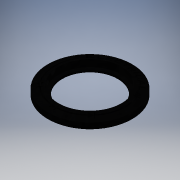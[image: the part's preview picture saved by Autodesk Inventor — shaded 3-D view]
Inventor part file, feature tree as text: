
AUTODESK INVENTOR PART (.ipt)
format: ipt  version: 2016 (Build 200138000, 138)  size: 675,840 bytes
history: native  units: in
note: dims shown in document units (in); Inventor stores cm internally (conversion verified against a paired STEP export)
features: sketch x3, extrude x2, projected_geometry x2, revolve x1
ambient origin geometry x8: Origin, YZ Plane, XZ Plane, XY Plane, X Axis, Y Axis, Z Axis, Center Point
bodies: Solid1 (feature_tree)
feature tree (8):
  revolve  "Revolution1"  [1 undecoded]
  extrude  "Extrusion1"  Depth=0.1in
  extrude  "Extrusion2"  Depth=0.275in
  sketch  "Sketch1"  dims[d0=0.8265in d1=0.175in]
  sketch  "Sketch2"  dims[d2=0.05in d3=0.1in]
  projected_geometry  "Projected Loop1"
  sketch  "Sketch3"  dims[d4=0.15in d5=0.275in d6=90.0deg d7=0.1in d18=0.05in d21=0.025in d22=0.125in d23=0.8in d24=0.025in d25=0.0125in d26=0.05in d27=0.025in d28=0.0125in d29=0.135in d30=0.135in d31=0.025in d32=0.025in d33=0.0125in d34=0.15in d35=0.05in d36=0.3in d37=0.025in d38=0.0125in d39=0.135in d40=0.3in d42=0.025in d43=0.135in d44=0.0451in d45=0.0451in d46=0.025in d47=0.0125in d48=0.05in d49=0.3in d50=0.025in d51=0.0125in d52=0.3in d53=0.135in d54=0.025in d55=0.135in d56=0.05in d57=0.025in d58=0.0125in d59=0.15in d60=0.135in d61=0.1in d62=0.075in d63=0.025in d64=0.025in d65=0.025in d66=0.8in d67=0.025in d68=0.0125in d69=0.1in d70=0.0in d71=0.075in d72=1.0in d73=0.0in]
  projected_geometry  "Projected Loop2"
note: 1 required parameter value undecoded (feature->parameter linkage not recoverable at this tier; creation-order binding heuristic only, values carry confidence <= 0.55)
